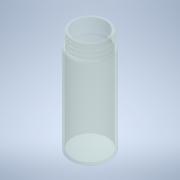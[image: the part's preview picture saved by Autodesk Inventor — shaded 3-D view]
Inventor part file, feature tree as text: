
AUTODESK INVENTOR PART (.ipt)
format: ipt  version: 2022 (Build 260153000, 153)  size: 240,640 bytes
history: native  units: mm
features: sketch x5, extrude x2, fillet x2, revolve x1, sweep x1, chamfer x1, other x1
ambient origin geometry x8: Origin, YZ Plane, XZ Plane, XY Plane, X Axis, Y Axis, Z Axis, Center Point
bodies: Solid1 (feature_tree)
feature tree (13):
  extrude  "Extrusion2"  Depth=1.5mm
  extrude  "Extrusion3"  Depth=1.5mm
  fillet  "Fillet3"  Radius=11.0mm
  revolve  "Revolution1"  Angle=90.0deg
  sweep  "Sweep1"
  chamfer  "Chamfer1"  Distance=1.0mm
  sketch  "Sketch2"  dims[d4=24.5mm d5=1.5mm]
  sketch  "Sketch3"  dims[d6=11.0mm d7=0.0mm d8=1.5mm d9=11.0mm d10=0.0mm]
  sketch  "Sketch4"  dims[d11=1.0mm d12=90.0deg]
  sketch  "Sketch5"  dims[d13=45.0deg d15=1.0mm d16=1.0mm d21=1.0mm d22=1.0mm d23=3.0mm d24=21.0mm d25=24.5mm d26=0.0mm d27=0.0mm d28=0.0mm d29=0.7mm d30=2.0mm d31=45.0deg]
  sketch  "3D Sketch2"
  other  "Helical Curve2"
  fillet  "Fillet1"  Radius=1.0mm
